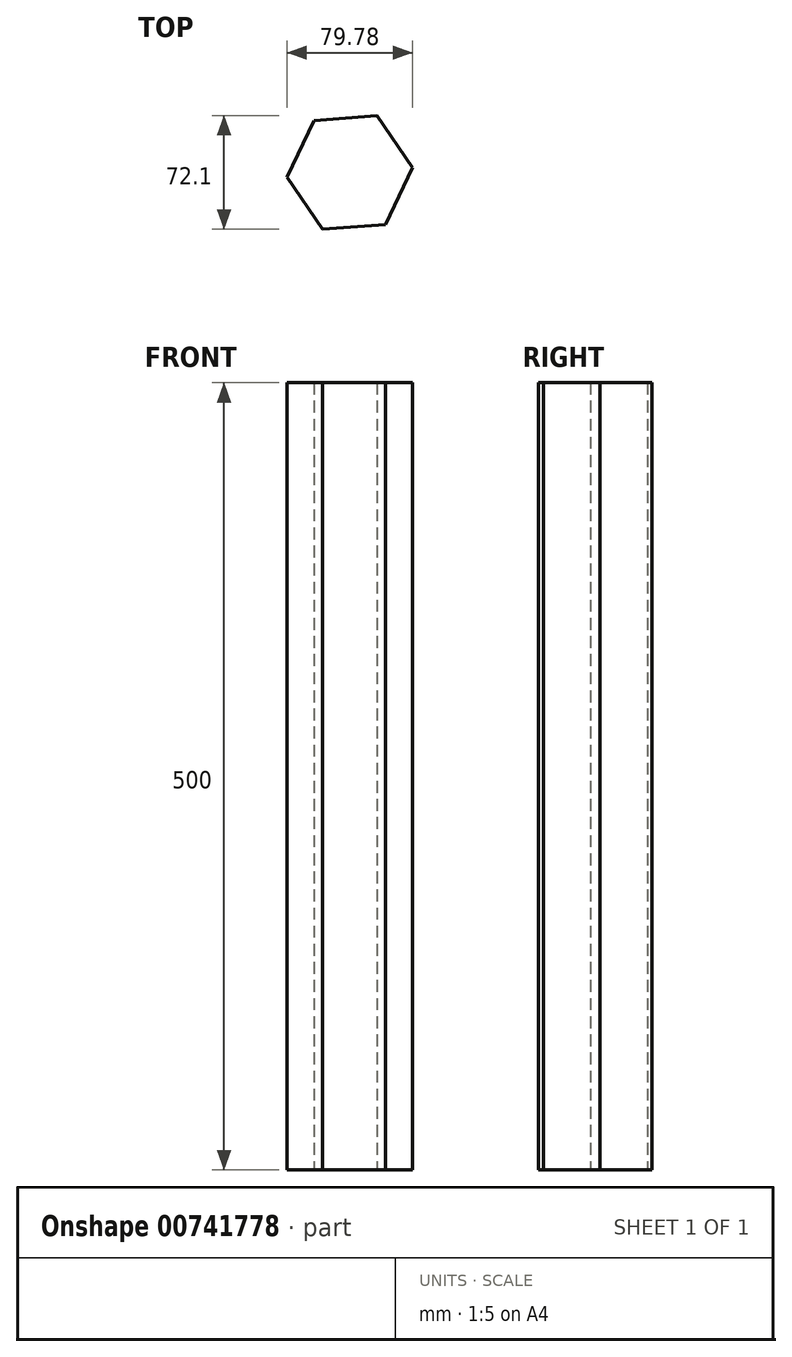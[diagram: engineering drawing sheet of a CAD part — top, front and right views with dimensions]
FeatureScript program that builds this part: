
annotation { "Feature Type Name" : "Feature", "Feature Type Description" : "" }
export const myFeature = defineFeature(function(context is Context, id is Id, definition is map)
    precondition{}
    {
        {
            var Q0;
            Q0=qCreatedBy(makeId("Top.planeOp"),FACE);
            var sketch = newSketch(context, id + "F0", { "sketchPlane" : qUnion([Q0])});
            skCircle(sketch, "E0.cCircle", {"center": v(0, 0) * mm, "radius": 34.64 * mm, "construction": true});
            skLineSegment(sketch, "E0.0", {"start": v(39.89, 3.02) * mm, "end": v(22.56, -33.03) * mm});
            skLineSegment(sketch, "E0.1", {"start": v(22.56, -33.03) * mm, "end": v(-17.32, -36.05) * mm});
            skLineSegment(sketch, "E0.2", {"start": v(-17.32, -36.05) * mm, "end": v(-39.89, -3.02) * mm});
            skLineSegment(sketch, "E0.3", {"start": v(-39.89, -3.02) * mm, "end": v(-22.56, 33.03) * mm});
            skLineSegment(sketch, "E0.4", {"start": v(-22.56, 33.03) * mm, "end": v(17.32, 36.05) * mm});
            skLineSegment(sketch, "E0.5", {"start": v(17.32, 36.05) * mm, "end": v(39.89, 3.02) * mm});
            skPoint(sketch, "E0.0.midPoint", {"position": v(31.22, -15) * mm});
            skSolve(sketch);
        }
        {
            var Q0;
            Q0 = qSketchRegion(id + "F0", true);
            extrude(context, id + "F1", {"entities" : qUnion([Q0]), "depth" : 500 * mm, "offsetDistance" : 25 * mm});
        }
    });
